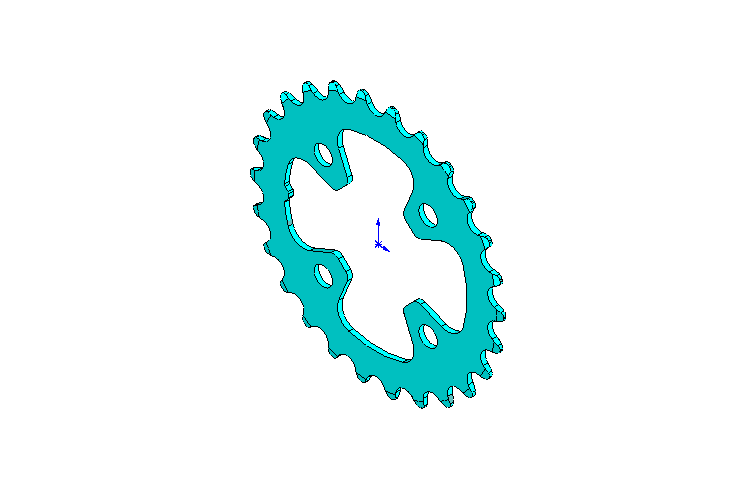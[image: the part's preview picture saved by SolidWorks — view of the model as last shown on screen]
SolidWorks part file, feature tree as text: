
SOLIDWORKS PART (.sldprt)
format: sldprt  version: not decoded by parser v0  size: 910,848 bytes
history: native  units: mm
features: sketch x5, plane x3, cut_extrude x3, material x1, extrude x1, cut_revolve x1, pattern_circular x1 (+10 scaffold rows collapsed)
feature tree (25):
  scaffold x10  (default folders/planes/origin — collapsed)
  material  "Matériau <non spécifié>"
  plane  "Plan de face"
  plane  "Plan de dessus"
  plane  "Plan de droite"
  sketch  "Esquisse1"  dims[D1=109.5mm]
  extrude  "Extrusion1"  Depth=2mm
  sketch  "Esquisse4"  dims[D1=2.5mm D2=1.0mm]
  cut_revolve  "Enlèvement de matière-Révolution1"  Angle=360deg
  sketch  "Esquisse2"  dims[c1.D1=8.0mm c1.D3=4.0mm c2.D1=8.0mm c2.D3=4.0mm c2.D4=1.5mm c3.D3=54.75mm c3.D2=9.5mm c4.D3=4.0mm c4.D2=~2.039916mm c5.D2=25.0deg c5.D3=2.0mm]
  cut_extrude  "Enlèv. mat.-Extru.1"  [1 undecoded]
  pattern_circular  "Répétition circulaire1"  Count=26 Angle=13.846154deg
  sketch  "Esquisse5"  dims[c1.D1=64.0mm c1.D2=8.0mm c1.D3=~32.724562mm c2.D3=90.0deg]
  cut_extrude  "Enlèv. mat.-Extru.2"  [1 undecoded]
  sketch  "Esquisse6"  dims[c1.D1=79.0mm c1.D2=41.0mm c1.D3=12.0mm c1.D4=41.0mm c1.D6=12.0mm c2.D3=7.0mm c2.D6=3.0mm c2.D8=39.5mm c2.D10=1.0mm c2.D2=20.5mm c2.D4=8.5mm c2.D5=~20.42608mm c3.D5=92.5deg c4.D5=~18.747483mm c5.D5=45.0deg c5.D2=41.0mm c5.D7=6.0mm c5.D8=2.0mm c5.D9=~1.885911mm c6.D9=90.0deg]
  cut_extrude  "Enlèv. mat.-Extru.3"  [1 undecoded]
decode coverage: 8 of 11 modeling features carry decoded parameters
note: ~ marks probable driven/reference dimensions
note: 3 parameter values undecoded
summary: no parameter record found for 3 features
note: suppression state not decoded; provenance and decode notes live in map.json
